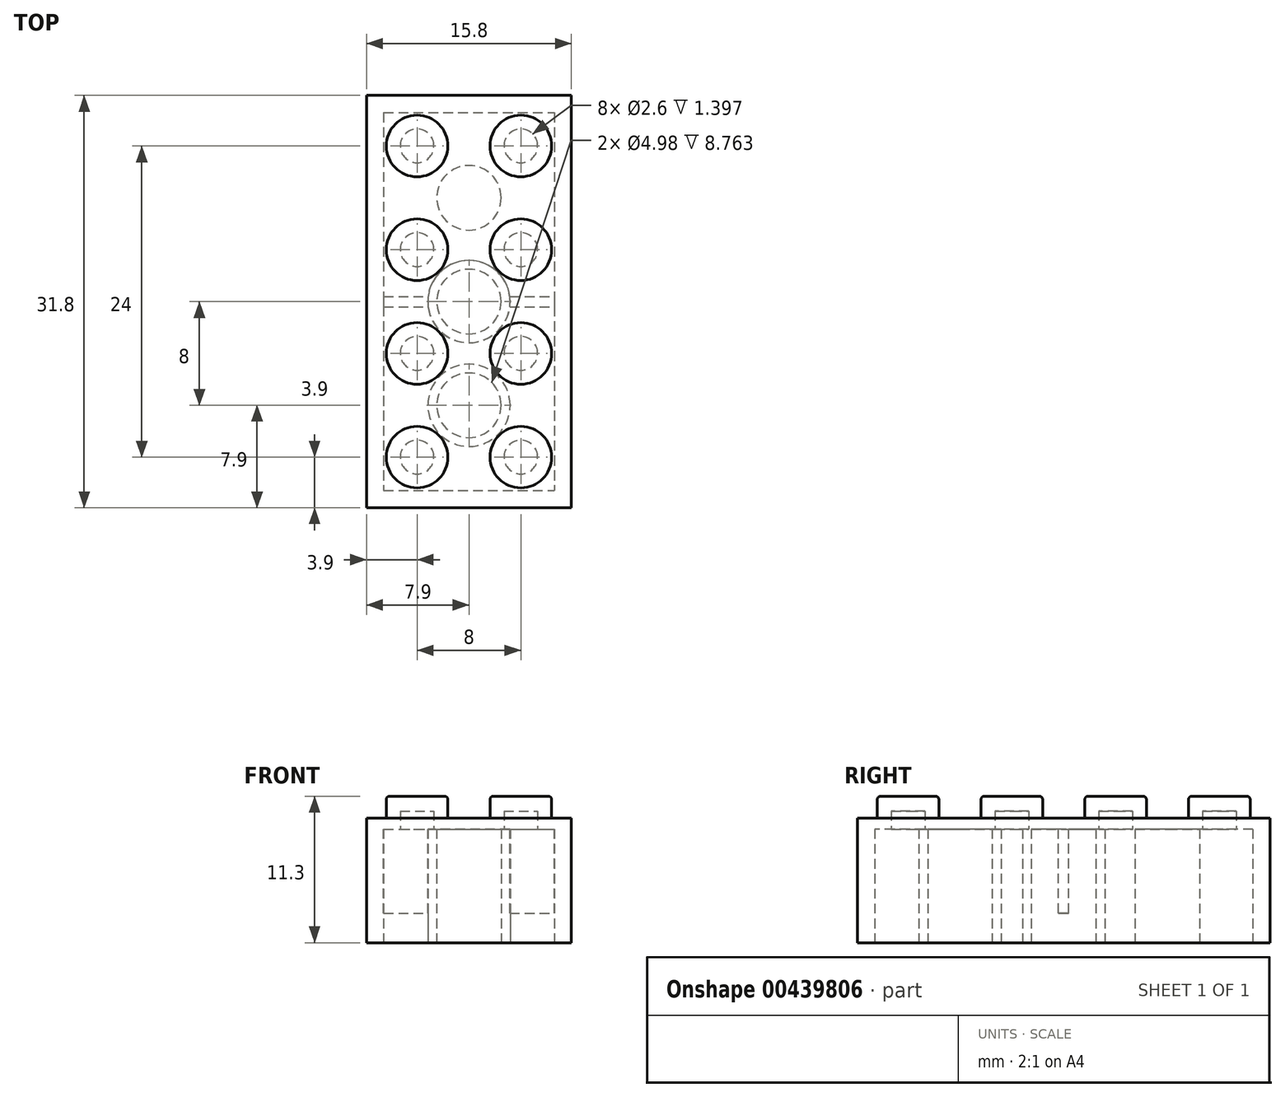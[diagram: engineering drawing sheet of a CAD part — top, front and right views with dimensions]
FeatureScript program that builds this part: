
annotation { "Feature Type Name" : "Feature", "Feature Type Description" : "" }
export const myFeature = defineFeature(function(context is Context, id is Id, definition is map)
    precondition{}
    {
        {
            var Q0;
            Q0=qCreatedBy(makeId("Top.planeOp"),FACE);
            var sketch = newSketch(context, id + "F0", { "sketchPlane" : qUnion([Q0])});
            skLineSegment(sketch, "E0.bottom", {"start": v(-15.8, -31.8) * mm, "end": v(0, -31.8) * mm});
            skLineSegment(sketch, "E0.top", {"start": v(-15.8, 0) * mm, "end": v(0, 0) * mm});
            skLineSegment(sketch, "E0.left", {"start": v(-15.8, -31.8) * mm, "end": v(-15.8, 0) * mm});
            skLineSegment(sketch, "E0.right", {"start": v(0, -31.8) * mm, "end": v(0, 0) * mm});
            skSolve(sketch);
        }
        {
            var Q0;
            Q0=makeQuery(id+"F0.imprint","IMPRINT",FACE,{"disambiguationData":[TD([[makeQuery(id+"F0.imprint","IMPRINT",EDGE,{"derivedFrom":sQuery(id+"F0.wireOp",EDGE,"E0.bottom")}),1.0]])]});
            extrude(context, id + "F1", {"entities" : qUnion([Q0]), "depth" : 9.6 * mm});
        }
        {
            var Q0;
            Q0=makeQuery(id+"F1.opExtrude","CAP_FACE",FACE,{"disambiguationData":[OSD([sQuery(id+"F0.wireOp",EDGE,"E0.bottom"),sQuery(id+"F0.wireOp",EDGE,"E0.top"),sQuery(id+"F0.wireOp",EDGE,"E0.left"),sQuery(id+"F0.wireOp",EDGE,"E0.right")])],"isStart":false});
            var sketch = newSketch(context, id + "F2", { "sketchPlane" : qUnion([Q0])});
            skCircle(sketch, "E1", {"center": v(-3.9, -3.9) * mm, "radius": 2.37 * mm});
            skCircle(sketch, "E2.0.1.0", {"center": v(-3.9, -11.9) * mm, "radius": 2.37 * mm});
            skCircle(sketch, "E2.0.2.0", {"center": v(-3.9, -19.9) * mm, "radius": 2.37 * mm});
            skCircle(sketch, "E2.0.3.0", {"center": v(-3.9, -27.9) * mm, "radius": 2.37 * mm});
            skCircle(sketch, "E2.1.0.0", {"center": v(-11.9, -3.9) * mm, "radius": 2.37 * mm});
            skCircle(sketch, "E2.1.1.0", {"center": v(-11.9, -11.9) * mm, "radius": 2.37 * mm});
            skCircle(sketch, "E2.1.2.0", {"center": v(-11.9, -19.9) * mm, "radius": 2.37 * mm});
            skCircle(sketch, "E2.1.3.0", {"center": v(-11.9, -27.9) * mm, "radius": 2.37 * mm});
            skLineSegment(sketch, "E2.direction1", {"start": v(-3.9, -3.9) * mm, "end": v(-11.9, -3.9) * mm, "construction": true});
            skLineSegment(sketch, "E2.direction2", {"start": v(-3.9, -3.9) * mm, "end": v(-3.9, -11.9) * mm, "construction": true});
            skSolve(sketch);
        }
        {
            var Q0;
            Q0 = qSketchRegion(id + "F2", true);
            extrude(context, id + "F3", {"entities" : qUnion([Q0]), "operationType" : NewBodyOperationType.ADD, "depth" : 1.7 * mm});
        }
        {
            var Q0;
            Q0=makeQuery(id+"F1.opExtrude","CAP_FACE",FACE,{"disambiguationData":[OSD([sQuery(id+"F0.wireOp",EDGE,"E0.bottom"),sQuery(id+"F0.wireOp",EDGE,"E0.top"),sQuery(id+"F0.wireOp",EDGE,"E0.left"),sQuery(id+"F0.wireOp",EDGE,"E0.right")])],"isStart":true});
            var sketch = newSketch(context, id + "F4", { "sketchPlane" : qUnion([Q0])});
            skLineSegment(sketch, "E3.bottom", {"start": v(-14.48, 1.32) * mm, "end": v(-1.32, 1.32) * mm});
            skLineSegment(sketch, "E3.top", {"start": v(-14.48, 30.48) * mm, "end": v(-1.32, 30.48) * mm});
            skLineSegment(sketch, "E3.left", {"start": v(-14.48, 1.32) * mm, "end": v(-14.48, 30.48) * mm});
            skLineSegment(sketch, "E3.right", {"start": v(-1.32, 1.32) * mm, "end": v(-1.32, 30.48) * mm});
            skCircle(sketch, "E4", {"center": v(-7.9, 23.9) * mm, "radius": 3.18 * mm});
            skCircle(sketch, "E5", {"center": v(-7.9, 15.9) * mm, "radius": 3.18 * mm});
            skCircle(sketch, "E6", {"center": v(-7.9, 15.9) * mm, "radius": 2.49 * mm});
            skCircle(sketch, "E7", {"center": v(-7.9, 23.9) * mm, "radius": 2.49 * mm});
            skLineSegment(sketch, "E8", {"start": v(-7.9, 1.32) * mm, "end": v(-7.9, 30.48) * mm, "construction": true});
            skLineSegment(sketch, "E9", {"start": v(-1.32, 15.9) * mm, "end": v(-14.48, 15.9) * mm, "construction": true});
            skLineSegment(sketch, "E10", {"start": v(-3.9, 27.9) * mm, "end": v(-11.9, 19.9) * mm, "construction": true});
            skCircle(sketch, "E11.MirrorC", {"center": v(-7.9, 7.9) * mm, "radius": 3.18 * mm});
            skCircle(sketch, "E12.MirrorC", {"center": v(-7.9, 7.9) * mm, "radius": 2.49 * mm});
            skSolve(sketch);
        }
        {
            var Q0;
            Q0 = qSketchRegion(id + "F4", true);
            extrude(context, id + "F5", {"entities" : qUnion([Q0]), "operationType" : NewBodyOperationType.REMOVE, "oppositeDirection" : true, "depth" : 8.76 * mm});
        }
        {
            var Q0;
            Q0=makeQuery(id+"F4.imprint","IMPRINT",FACE,{"disambiguationData":[TD([[makeQuery(id+"F4.imprint","IMPRINT",EDGE,{"derivedFrom":sQuery(id+"F4.wireOp",EDGE,"E7")}),1.0]])]});
            var Q1;
            Q1=makeQuery(id+"F4.imprint","IMPRINT",FACE,{"disambiguationData":[TD([[makeQuery(id+"F4.imprint","IMPRINT",EDGE,{"derivedFrom":sQuery(id+"F4.wireOp",EDGE,"E6")}),1.0]])]});
            var Q2;
            Q2=makeQuery(id+"F4.imprint","IMPRINT",FACE,{"disambiguationData":[TD([[makeQuery(id+"F4.imprint","IMPRINT",EDGE,{"derivedFrom":sQuery(id+"F4.wireOp",EDGE,"ewNiTv9N-kwH8-zp8D-8VmK-iinGs2Req3qf")}),1.0]])]});
            var Q3;
            Q3=makeQuery(id+"F4.imprint","IMPRINT",FACE,{"disambiguationData":[TD([[makeQuery(id+"F4.imprint","IMPRINT",EDGE,{"derivedFrom":sQuery(id+"F4.wireOp",EDGE,"E12.MirrorC")}),-1.0]])]});
            extrude(context, id + "F6", {"entities" : qUnion([Q0, Q1, Q2, Q3]), "operationType" : NewBodyOperationType.REMOVE, "oppositeDirection" : true, "depth" : 8.76 * mm});
        }
        {
            var Q0;
            Q0=makeQuery(id+"F5.boolean.opBoolean","COPY",FACE,{"derivedFrom":makeQuery(id+"F5.opExtrude","CAP_FACE",FACE,{"disambiguationData":[OSD([sQuery(id+"F4.wireOp",EDGE,"E3.bottom"),sQuery(id+"F4.wireOp",EDGE,"E3.top"),sQuery(id+"F4.wireOp",EDGE,"E3.left"),sQuery(id+"F4.wireOp",EDGE,"E3.right"),sQuery(id+"F4.wireOp",EDGE,"E4"),sQuery(id+"F4.wireOp",EDGE,"E5"),sQuery(id+"F4.wireOp",EDGE,"eTSD7xsl-GOij-G5rq-uAMM-qAvroOvZzWVF")])],"isStart":false})});
            var sketch = newSketch(context, id + "F7", { "sketchPlane" : qUnion([Q0])});
            skLineSegment(sketch, "E13", {"start": v(-14.48, 15.9) * mm, "end": v(-1.32, 15.9) * mm, "construction": true});
            skLineSegment(sketch, "E14.bottom", {"start": v(-14.48, 16.3) * mm, "end": v(-10.76, 16.3) * mm});
            skLineSegment(sketch, "E14.top", {"start": v(-14.48, 15.5) * mm, "end": v(-10.76, 15.5) * mm});
            skLineSegment(sketch, "E14.left", {"start": v(-14.48, 16.3) * mm, "end": v(-14.48, 15.5) * mm});
            skLineSegment(sketch, "E14.right", {"start": v(-10.76, 16.3) * mm, "end": v(-10.76, 15.5) * mm});
            skLineSegment(sketch, "E15.bottom", {"start": v(-5.03, 16.3) * mm, "end": v(-1.32, 16.3) * mm});
            skLineSegment(sketch, "E15.top", {"start": v(-5.03, 15.5) * mm, "end": v(-1.32, 15.5) * mm});
            skLineSegment(sketch, "E15.left", {"start": v(-5.03, 16.3) * mm, "end": v(-5.03, 15.5) * mm});
            skLineSegment(sketch, "E15.right", {"start": v(-1.32, 16.3) * mm, "end": v(-1.32, 15.5) * mm});
            skSolve(sketch);
        }
        {
            var Q0;
            {var subQ0=sQuery(id+"F7.wireOp",EDGE,"E15.right");Q0=makeQuery(id+"F7.imprint","IMPRINT",FACE,{"disambiguationData":[TD([[makeQuery(id+"F7.imprint","IMPRINT",EDGE,{"derivedFrom":subQ0}),1.0]])]});}
            var Q1;
            {var subQ0=sQuery(id+"F7.wireOp",EDGE,"E14.left");Q1=makeQuery(id+"F7.imprint","IMPRINT",FACE,{"disambiguationData":[TD([[makeQuery(id+"F7.imprint","IMPRINT",EDGE,{"derivedFrom":subQ0}),-1.0]])]});}
            var Q2;
            {var subQ0=sQuery(id+"F0.wireOp",EDGE,"E0.left");var subQ1=sQuery(id+"F0.wireOp",EDGE,"E0.top");var subQ2=sQuery(id+"F0.wireOp",EDGE,"E0.right");var subQ3=sQuery(id+"F0.wireOp",EDGE,"E0.bottom");Q2=makeQuery(id+"F5.boolean.opBoolean","SPLIT",FACE,{"disambiguationData":[TD([makeQuery(id+"F1.opExtrude","SWEPT_FACE",FACE,{"disambiguationData":[OSD([subQ3])]})])],"derivedFrom":makeQuery(id+"F1.opExtrude","CAP_FACE",FACE,{"disambiguationData":[OSD([subQ3,subQ1,subQ0,subQ2])],"isStart":true})});}
            extrude(context, id + "F8", {"entities" : qUnion([Q0, Q1]), "operationType" : NewBodyOperationType.ADD, "endBoundEntityFace" : qUnion([Q2]), "depth" : 6.48 * mm});
        }
        {
            var Q0;
            {var subQ0=sQuery(id+"F4.wireOp",EDGE,"E4");var subQ1=sQuery(id+"F4.wireOp",EDGE,"E3.right");var subQ2=sQuery(id+"F4.wireOp",EDGE,"E3.left");var subQ3=sQuery(id+"F4.wireOp",EDGE,"E3.top");var subQ4=sQuery(id+"F4.wireOp",EDGE,"E5");Q0=makeQuery(id+"F8.boolean.opBoolean","SPLIT",FACE,{"disambiguationData":[TD([makeQuery(id+"F5.boolean.opBoolean","COPY",FACE,{"derivedFrom":makeQuery(id+"F5.opExtrude","SWEPT_FACE",FACE,{"disambiguationData":[OSD([subQ3])]})})])],"derivedFrom":makeQuery(id+"F5.boolean.opBoolean","COPY",FACE,{"derivedFrom":makeQuery(id+"F5.opExtrude","CAP_FACE",FACE,{"disambiguationData":[OSD([sQuery(id+"F4.wireOp",EDGE,"E3.bottom"),subQ3,subQ2,subQ1,subQ0,subQ4,sQuery(id+"F4.wireOp",EDGE,"eTSD7xsl-GOij-G5rq-uAMM-qAvroOvZzWVF")])],"isStart":false})})});}
            var sketch = newSketch(context, id + "F9", { "sketchPlane" : qUnion([Q0])});
            skCircle(sketch, "E16", {"center": v(-11.9, 3.9) * mm, "radius": 1.3 * mm});
            skCircle(sketch, "E17.0.1.0", {"center": v(-11.9, 11.9) * mm, "radius": 1.3 * mm});
            skCircle(sketch, "E17.0.2.0", {"center": v(-11.9, 19.9) * mm, "radius": 1.3 * mm});
            skCircle(sketch, "E17.0.3.0", {"center": v(-11.9, 27.9) * mm, "radius": 1.3 * mm});
            skCircle(sketch, "E17.1.0.0", {"center": v(-3.9, 3.9) * mm, "radius": 1.3 * mm});
            skCircle(sketch, "E17.1.1.0", {"center": v(-3.9, 11.9) * mm, "radius": 1.3 * mm});
            skCircle(sketch, "E17.1.2.0", {"center": v(-3.9, 19.9) * mm, "radius": 1.3 * mm});
            skCircle(sketch, "E17.1.3.0", {"center": v(-3.9, 27.9) * mm, "radius": 1.3 * mm});
            skLineSegment(sketch, "E17.direction1", {"start": v(-11.9, 3.9) * mm, "end": v(-3.9, 3.9) * mm, "construction": true});
            skLineSegment(sketch, "E17.direction2", {"start": v(-11.9, 3.9) * mm, "end": v(-11.9, 11.9) * mm, "construction": true});
            skSolve(sketch);
        }
        {
            var Q0;
            Q0 = qSketchRegion(id + "F9", true);
            extrude(context, id + "F10", {"entities" : qUnion([Q0]), "operationType" : NewBodyOperationType.REMOVE, "oppositeDirection" : true, "depth" : 1.4 * mm});
        }
        {
            var Q0;
            Q0=makeQuery(id+"F3.opExtrude","CAP_EDGE",EDGE,{"disambiguationData":[OSD([sQuery(id+"F2.wireOp",EDGE,"E2.1.0.0")])],"isStart":false});
            var Q1;
            Q1=makeQuery(id+"F3.opExtrude","CAP_EDGE",EDGE,{"disambiguationData":[OSD([sQuery(id+"F2.wireOp",EDGE,"E1")])],"isStart":false});
            var Q2;
            Q2=makeQuery(id+"F3.opExtrude","CAP_EDGE",EDGE,{"disambiguationData":[OSD([sQuery(id+"F2.wireOp",EDGE,"E2.1.1.0")])],"isStart":false});
            var Q3;
            Q3=makeQuery(id+"F3.opExtrude","CAP_EDGE",EDGE,{"disambiguationData":[OSD([sQuery(id+"F2.wireOp",EDGE,"E2.1.2.0")])],"isStart":false});
            var Q4;
            Q4=makeQuery(id+"F3.opExtrude","CAP_EDGE",EDGE,{"disambiguationData":[OSD([sQuery(id+"F2.wireOp",EDGE,"E2.0.1.0")])],"isStart":false});
            var Q5;
            Q5=makeQuery(id+"F3.opExtrude","CAP_EDGE",EDGE,{"disambiguationData":[OSD([sQuery(id+"F2.wireOp",EDGE,"E2.0.2.0")])],"isStart":false});
            var Q6;
            Q6=makeQuery(id+"F3.opExtrude","CAP_EDGE",EDGE,{"disambiguationData":[OSD([sQuery(id+"F2.wireOp",EDGE,"E2.1.3.0")])],"isStart":false});
            var Q7;
            Q7=makeQuery(id+"F3.opExtrude","CAP_EDGE",EDGE,{"disambiguationData":[OSD([sQuery(id+"F2.wireOp",EDGE,"E2.0.3.0")])],"isStart":false});
            fillet(context, id + "F11", {"entities" : qUnion([Q0, Q1, Q2, Q3, Q4, Q5, Q6, Q7]), "radius" : 0.25 * mm, "tangentPropagation" : true, "allowEdgeOverflow" : false});
        }
    });
